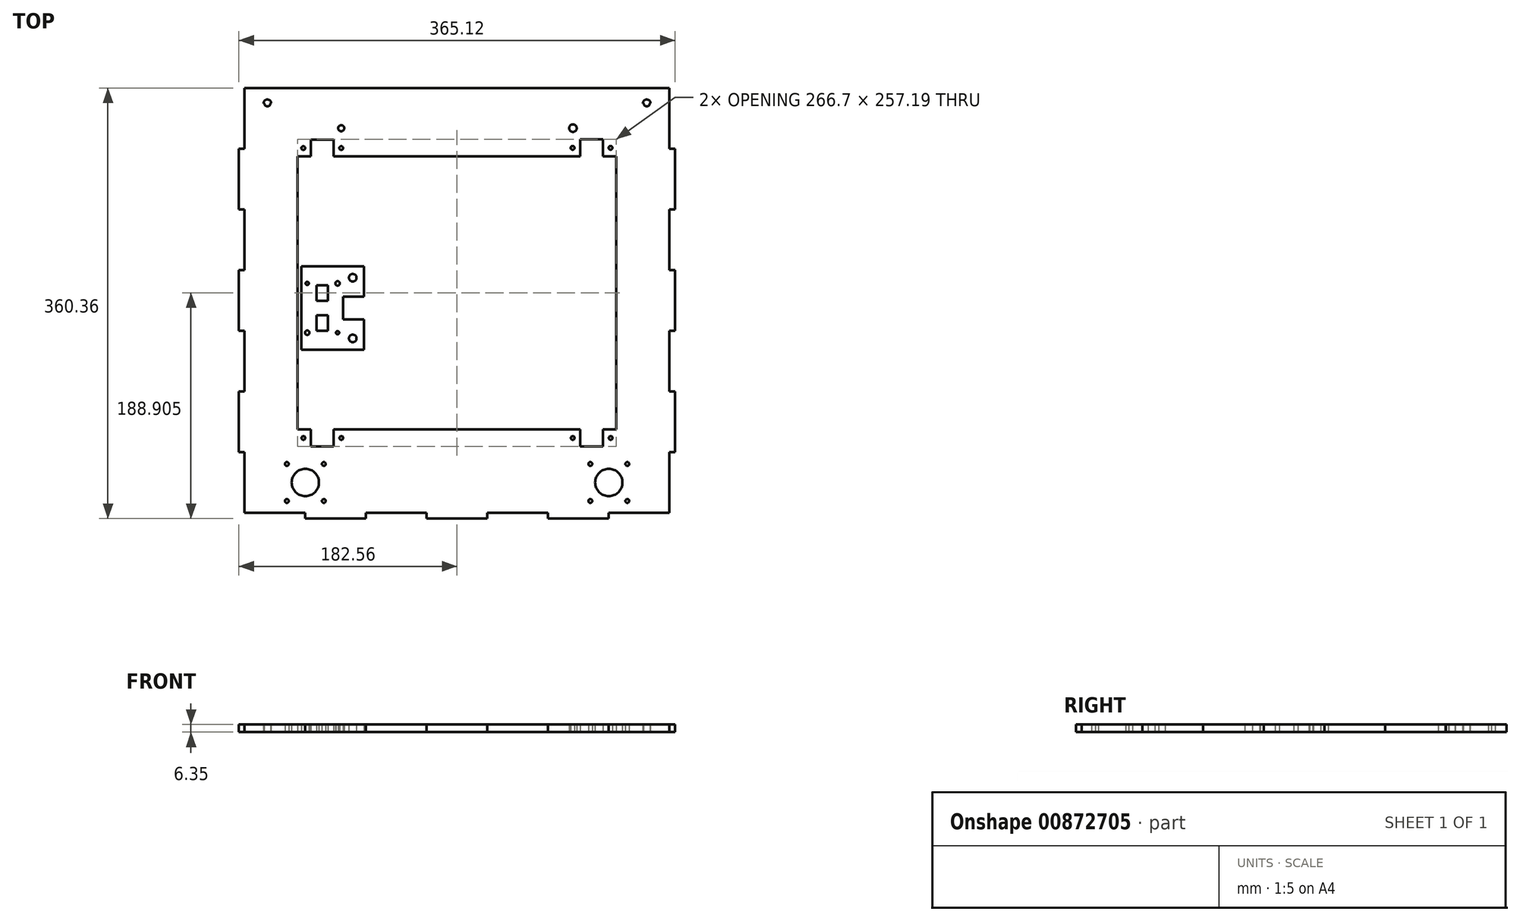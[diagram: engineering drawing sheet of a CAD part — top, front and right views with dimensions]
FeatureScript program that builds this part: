
annotation { "Feature Type Name" : "Feature", "Feature Type Description" : "" }
export const myFeature = defineFeature(function(context is Context, id is Id, definition is map)
    precondition{}
    {
        {
            var Q0;
            Q0=qCreatedBy(makeId("Top.planeOp"),FACE);
            var sketch = newSketch(context, id + "F0", { "sketchPlane" : qUnion([Q0])});
            skLineSegment(sketch, "E0.bottom", {"start": v(-177.8, 171.45) * mm, "end": v(177.8, 171.45) * mm});
            skLineSegment(sketch, "E0.top", {"start": v(-177.8, -171.45) * mm, "end": v(177.8, -171.45) * mm});
            skLineSegment(sketch, "E0.left", {"start": v(-177.8, 171.45) * mm, "end": v(-177.8, -171.45) * mm});
            skLineSegment(sketch, "E0.right", {"start": v(177.8, 171.45) * mm, "end": v(177.8, -171.45) * mm});
            skPoint(sketch, "E0.middle", {"position": v(0, 0) * mm});
            skLineSegment(sketch, "E1.0", {"start": v(-133.35, -101.6) * mm, "end": v(133.35, -101.6) * mm});
            skLineSegment(sketch, "E2.0", {"start": v(-133.35, 127) * mm, "end": v(-133.35, -101.6) * mm});
            skLineSegment(sketch, "E3", {"start": v(0, 171.45) * mm, "end": v(0, -171.45) * mm, "construction": true});
            skLineSegment(sketch, "E4", {"start": v(-177.8, 0) * mm, "end": v(177.8, 0) * mm, "construction": true});
            skLineSegment(sketch, "E5.MirrorCS", {"start": v(133.35, 127) * mm, "end": v(133.35, -101.6) * mm});
            skLineSegment(sketch, "E6.0", {"start": v(-133.35, 127) * mm, "end": v(133.35, 127) * mm});
            skLineSegment(sketch, "E7.bottom", {"start": v(-130.18, 25.4) * mm, "end": v(-95.25, 25.4) * mm});
            skLineSegment(sketch, "E7.top", {"start": v(-130.18, -25.4) * mm, "end": v(-95.25, -25.4) * mm});
            skLineSegment(sketch, "E7.left", {"start": v(-130.18, 25.4) * mm, "end": v(-130.18, -25.4) * mm});
            skLineSegment(sketch, "E7.right", {"start": v(-95.25, 25.4) * mm, "end": v(-95.25, -25.4) * mm});
            skLineSegment(sketch, "E8", {"start": v(-112.71, 25.4) * mm, "end": v(-112.71, -171.45) * mm, "construction": true});
            skLineSegment(sketch, "E9.bottom", {"start": v(-107.95, 6.1) * mm, "end": v(-117.48, 6.1) * mm});
            skLineSegment(sketch, "E9.top", {"start": v(-107.95, 19.05) * mm, "end": v(-117.48, 19.05) * mm});
            skLineSegment(sketch, "E9.left", {"start": v(-107.95, 6.1) * mm, "end": v(-107.95, 19.05) * mm});
            skLineSegment(sketch, "E9.right", {"start": v(-117.48, 6.1) * mm, "end": v(-117.48, 19.05) * mm});
            skPoint(sketch, "E9.middle", {"position": v(-112.71, 12.57) * mm});
            skPoint(sketch, "E10", {"position": v(-95.25, 0) * mm});
            skLineSegment(sketch, "E11.MirrorCS", {"start": v(-117.48, -6.1) * mm, "end": v(-117.48, -19.05) * mm});
            skLineSegment(sketch, "E12.MirrorCS", {"start": v(-107.95, -6.1) * mm, "end": v(-107.95, -19.05) * mm});
            skPoint(sketch, "E13.MirrorP", {"position": v(-112.71, -12.57) * mm});
            skLineSegment(sketch, "E14.MirrorCS", {"start": v(-107.95, -6.1) * mm, "end": v(-117.48, -6.1) * mm});
            skLineSegment(sketch, "E15.MirrorCS", {"start": v(-107.95, -19.05) * mm, "end": v(-117.48, -19.05) * mm});
            skCircle(sketch, "E16", {"center": v(-127, -146.05) * mm, "radius": 11.43 * mm});
            skCircle(sketch, "E17", {"center": v(-111.5, -130.56) * mm, "radius": 1.59 * mm});
            skCircle(sketch, "E18.1.0", {"center": v(-142.5, -130.56) * mm, "radius": 1.59 * mm});
            skCircle(sketch, "E18.2.0", {"center": v(-142.5, -161.54) * mm, "radius": 1.59 * mm});
            skCircle(sketch, "E18.3.0", {"center": v(-111.5, -161.54) * mm, "radius": 1.59 * mm});
            skCircle(sketch, "E19.MirrorC", {"center": v(142.5, -130.56) * mm, "radius": 1.59 * mm});
            skCircle(sketch, "E20.MirrorC", {"center": v(111.5, -130.56) * mm, "radius": 1.59 * mm});
            skCircle(sketch, "E21.MirrorC", {"center": v(142.5, -161.54) * mm, "radius": 1.59 * mm});
            skPoint(sketch, "E22.MirrorP", {"position": v(127, -146.05) * mm});
            skCircle(sketch, "E23.MirrorC", {"center": v(111.5, -161.54) * mm, "radius": 1.59 * mm});
            skCircle(sketch, "E24.MirrorC", {"center": v(127, -146.05) * mm, "radius": 11.43 * mm});
            skPoint(sketch, "E25.orphan", {"position": v(-112.71, -25.4) * mm});
            skCircle(sketch, "E26", {"center": v(-128.59, -108.75) * mm, "radius": 1.59 * mm});
            skCircle(sketch, "E27.MirrorC", {"center": v(-96.84, -108.75) * mm, "radius": 1.59 * mm});
            skLineSegment(sketch, "E28.bottom", {"start": v(-122.24, -101.6) * mm, "end": v(-103.19, -101.6) * mm});
            skLineSegment(sketch, "E28.top", {"start": v(-122.24, -115.9) * mm, "end": v(-103.19, -115.9) * mm});
            skLineSegment(sketch, "E28.left", {"start": v(-122.24, -101.6) * mm, "end": v(-122.24, -115.9) * mm});
            skLineSegment(sketch, "E28.right", {"start": v(-103.19, -101.6) * mm, "end": v(-103.19, -115.9) * mm});
            skPoint(sketch, "E29", {"position": v(-112.71, -115.9) * mm});
            skLineSegment(sketch, "E30.MirrorCS", {"start": v(122.24, -101.6) * mm, "end": v(122.24, -115.9) * mm});
            skCircle(sketch, "E31.MirrorC", {"center": v(96.84, -108.75) * mm, "radius": 1.59 * mm});
            skCircle(sketch, "E32.MirrorC", {"center": v(128.59, -108.75) * mm, "radius": 1.59 * mm});
            skLineSegment(sketch, "E33.MirrorCS", {"start": v(122.24, -101.6) * mm, "end": v(103.19, -101.6) * mm});
            skPoint(sketch, "E34.MirrorP", {"position": v(112.71, -115.9) * mm});
            skLineSegment(sketch, "E35.MirrorCS", {"start": v(103.19, -101.6) * mm, "end": v(103.19, -115.9) * mm});
            skLineSegment(sketch, "E36.MirrorCS", {"start": v(122.24, -115.9) * mm, "end": v(103.19, -115.9) * mm});
            skLineSegment(sketch, "E37", {"start": v(133.35, 12.7) * mm, "end": v(-133.35, 12.57) * mm, "construction": true});
            skCircle(sketch, "E38.MirrorC", {"center": v(-128.7, 133.9) * mm, "radius": 1.59 * mm});
            skLineSegment(sketch, "E39.MirrorCS", {"start": v(-122.36, 141.06) * mm, "end": v(-103.3, 141.07) * mm});
            skLineSegment(sketch, "E40.MirrorCS", {"start": v(-122.35, 126.76) * mm, "end": v(-103.3, 126.77) * mm});
            skCircle(sketch, "E41.MirrorC", {"center": v(128.47, 134.15) * mm, "radius": 1.59 * mm});
            skLineSegment(sketch, "E42.MirrorCS", {"start": v(-122.35, 126.76) * mm, "end": v(-122.36, 141.06) * mm});
            skCircle(sketch, "E43.MirrorC", {"center": v(-96.95, 133.93) * mm, "radius": 1.59 * mm});
            skLineSegment(sketch, "E44.MirrorCS", {"start": v(122.12, 141.29) * mm, "end": v(103.07, 141.27) * mm});
            skCircle(sketch, "E45.MirrorC", {"center": v(96.72, 134.12) * mm, "radius": 1.59 * mm});
            skLineSegment(sketch, "E46.MirrorCS", {"start": v(122.13, 126.99) * mm, "end": v(103.08, 126.97) * mm});
            skPoint(sketch, "E47.MirrorP", {"position": v(-112.83, 141.07) * mm});
            skPoint(sketch, "E48.MirrorP", {"position": v(112.6, 141.28) * mm});
            skLineSegment(sketch, "E49.MirrorCS", {"start": v(-133.46, 126.75) * mm, "end": v(133.24, 127) * mm});
            skLineSegment(sketch, "E50.MirrorCS", {"start": v(103.08, 126.97) * mm, "end": v(103.07, 141.27) * mm});
            skLineSegment(sketch, "E51.MirrorCS", {"start": v(-103.3, 126.77) * mm, "end": v(-103.3, 141.07) * mm});
            skLineSegment(sketch, "E52.MirrorCS", {"start": v(122.13, 126.99) * mm, "end": v(122.12, 141.29) * mm});
            skLineSegment(sketch, "E53.bottom", {"start": v(-95.25, -9.53) * mm, "end": v(-77.79, -9.53) * mm});
            skLineSegment(sketch, "E53.top", {"start": v(-95.25, 9.52) * mm, "end": v(-77.79, 9.52) * mm});
            skLineSegment(sketch, "E53.left", {"start": v(-95.25, -9.53) * mm, "end": v(-95.25, 9.52) * mm});
            skLineSegment(sketch, "E53.right", {"start": v(-77.79, -9.53) * mm, "end": v(-77.79, 9.52) * mm});
            skPoint(sketch, "E54", {"position": v(-65.09, 0) * mm});
            skLineSegment(sketch, "E55.bottom", {"start": v(-95.25, -25.4) * mm, "end": v(-77.79, -25.4) * mm});
            skLineSegment(sketch, "E55.top", {"start": v(-95.25, 25.4) * mm, "end": v(-77.79, 25.4) * mm});
            skLineSegment(sketch, "E55.left", {"start": v(-95.25, -25.4) * mm, "end": v(-95.25, 25.4) * mm});
            skLineSegment(sketch, "E55.right", {"start": v(-77.79, -25.4) * mm, "end": v(-77.79, 25.4) * mm});
            skLineSegment(sketch, "E56.0", {"start": v(-100.01, 34.92) * mm, "end": v(-77.79, 34.92) * mm});
            skLineSegment(sketch, "E56.1", {"start": v(-130.18, 34.92) * mm, "end": v(-100.01, 34.92) * mm});
            skLineSegment(sketch, "E57", {"start": v(-77.79, 34.92) * mm, "end": v(-77.79, 25.4) * mm});
            skLineSegment(sketch, "E58", {"start": v(-130.18, 25.4) * mm, "end": v(-130.18, 34.92) * mm});
            skLineSegment(sketch, "E59.MirrorCS", {"start": v(-130.18, -25.4) * mm, "end": v(-130.18, -34.92) * mm});
            skLineSegment(sketch, "E60.MirrorCS", {"start": v(-100.01, -34.93) * mm, "end": v(-77.79, -34.93) * mm});
            skLineSegment(sketch, "E61.MirrorCS", {"start": v(-130.18, -34.93) * mm, "end": v(-100.01, -34.93) * mm});
            skLineSegment(sketch, "E62.MirrorCS", {"start": v(-77.79, -34.92) * mm, "end": v(-77.79, -25.4) * mm});
            skCircle(sketch, "E63", {"center": v(-87.31, 25.4) * mm, "radius": 3.18 * mm});
            skCircle(sketch, "E64.MirrorC", {"center": v(-87.31, -25.4) * mm, "radius": 3.18 * mm});
            skCircle(sketch, "E65", {"center": v(-125.41, 20.64) * mm, "radius": 1.84 * mm});
            skCircle(sketch, "E66.MirrorC", {"center": v(-100.01, 20.64) * mm, "radius": 1.84 * mm});
            skCircle(sketch, "E67.MirrorC", {"center": v(-125.41, -20.64) * mm, "radius": 1.84 * mm});
            skCircle(sketch, "E68.MirrorC", {"center": v(-100.01, -20.64) * mm, "radius": 1.84 * mm});
            skCircle(sketch, "E69", {"center": v(-158.75, 171.45) * mm, "radius": 3.18 * mm});
            skCircle(sketch, "E70", {"center": v(-96.95, 150.6) * mm, "radius": 3.18 * mm});
            skCircle(sketch, "E71.MirrorC", {"center": v(96.95, 150.6) * mm, "radius": 3.18 * mm});
            skCircle(sketch, "E72.MirrorC", {"center": v(158.75, 171.45) * mm, "radius": 3.18 * mm});
            skLineSegment(sketch, "E73.0", {"start": v(-177.8, 184.15) * mm, "end": v(177.8, 184.15) * mm});
            skLineSegment(sketch, "E74", {"start": v(-177.8, 171.45) * mm, "end": v(-177.8, 184.15) * mm});
            skLineSegment(sketch, "E75", {"start": v(177.8, 171.45) * mm, "end": v(177.8, 184.15) * mm});
            skLineSegment(sketch, "E76.bottom", {"start": v(-177.8, 133.35) * mm, "end": v(-182.56, 133.35) * mm});
            skLineSegment(sketch, "E76.top", {"start": v(-177.8, 82.55) * mm, "end": v(-182.56, 82.55) * mm});
            skLineSegment(sketch, "E76.left", {"start": v(-177.8, 133.35) * mm, "end": v(-177.8, 82.55) * mm});
            skLineSegment(sketch, "E76.right", {"start": v(-182.56, 133.35) * mm, "end": v(-182.56, 82.55) * mm});
            skLineSegment(sketch, "E77.bottom", {"start": v(-177.8, 31.75) * mm, "end": v(-182.56, 31.75) * mm});
            skLineSegment(sketch, "E77.top", {"start": v(-177.8, -19.05) * mm, "end": v(-182.56, -19.05) * mm});
            skLineSegment(sketch, "E77.left", {"start": v(-177.8, 31.75) * mm, "end": v(-177.8, -19.05) * mm});
            skLineSegment(sketch, "E77.right", {"start": v(-182.56, 31.75) * mm, "end": v(-182.56, -19.05) * mm});
            skLineSegment(sketch, "E78.bottom", {"start": v(-177.8, -69.85) * mm, "end": v(-182.56, -69.85) * mm});
            skLineSegment(sketch, "E78.top", {"start": v(-177.8, -120.65) * mm, "end": v(-182.56, -120.65) * mm});
            skLineSegment(sketch, "E78.left", {"start": v(-177.8, -69.85) * mm, "end": v(-177.8, -120.65) * mm});
            skLineSegment(sketch, "E78.right", {"start": v(-182.56, -69.85) * mm, "end": v(-182.56, -120.65) * mm});
            skLineSegment(sketch, "E79.MirrorCS", {"start": v(177.8, -120.65) * mm, "end": v(182.56, -120.65) * mm});
            skLineSegment(sketch, "E80.MirrorCS", {"start": v(177.8, 31.75) * mm, "end": v(182.56, 31.75) * mm});
            skLineSegment(sketch, "E81.MirrorCS", {"start": v(177.8, -19.05) * mm, "end": v(182.56, -19.05) * mm});
            skLineSegment(sketch, "E82.MirrorCS", {"start": v(177.8, 82.55) * mm, "end": v(182.56, 82.55) * mm});
            skLineSegment(sketch, "E83.MirrorCS", {"start": v(177.8, -69.85) * mm, "end": v(182.56, -69.85) * mm});
            skLineSegment(sketch, "E84.MirrorCS", {"start": v(177.8, 133.35) * mm, "end": v(182.56, 133.35) * mm});
            skLineSegment(sketch, "E85.MirrorCS", {"start": v(182.56, 133.35) * mm, "end": v(182.56, 82.55) * mm});
            skLineSegment(sketch, "E86.MirrorCS", {"start": v(177.8, 31.75) * mm, "end": v(177.8, -19.05) * mm});
            skLineSegment(sketch, "E87.MirrorCS", {"start": v(182.56, 31.75) * mm, "end": v(182.56, -19.05) * mm});
            skLineSegment(sketch, "E88.MirrorCS", {"start": v(177.8, 133.35) * mm, "end": v(177.8, 82.55) * mm});
            skLineSegment(sketch, "E89.MirrorCS", {"start": v(177.8, -69.85) * mm, "end": v(177.8, -120.65) * mm});
            skLineSegment(sketch, "E90.MirrorCS", {"start": v(182.56, -69.85) * mm, "end": v(182.56, -120.65) * mm});
            skLineSegment(sketch, "E91.bottom", {"start": v(-127, 184.15) * mm, "end": v(-76.2, 184.15) * mm});
            skLineSegment(sketch, "E91.top", {"start": v(-127, 188.91) * mm, "end": v(-76.2, 188.91) * mm});
            skLineSegment(sketch, "E91.left", {"start": v(-127, 184.15) * mm, "end": v(-127, 188.91) * mm});
            skLineSegment(sketch, "E91.right", {"start": v(-76.2, 184.15) * mm, "end": v(-76.2, 188.91) * mm});
            skLineSegment(sketch, "E92.bottom", {"start": v(-25.4, 184.15) * mm, "end": v(25.4, 184.15) * mm});
            skLineSegment(sketch, "E92.top", {"start": v(-25.4, 188.91) * mm, "end": v(25.4, 188.91) * mm});
            skLineSegment(sketch, "E92.left", {"start": v(-25.4, 184.15) * mm, "end": v(-25.4, 188.91) * mm});
            skLineSegment(sketch, "E92.right", {"start": v(25.4, 184.15) * mm, "end": v(25.4, 188.91) * mm});
            skLineSegment(sketch, "E93.bottom", {"start": v(76.2, 184.15) * mm, "end": v(127, 184.15) * mm});
            skLineSegment(sketch, "E93.top", {"start": v(76.2, 188.91) * mm, "end": v(127, 188.91) * mm});
            skLineSegment(sketch, "E93.left", {"start": v(76.2, 184.15) * mm, "end": v(76.2, 188.91) * mm});
            skLineSegment(sketch, "E93.right", {"start": v(127, 184.15) * mm, "end": v(127, 188.91) * mm});
            skLineSegment(sketch, "E94", {"start": v(177.8, 184.15) * mm, "end": v(177.8, -171.45) * mm, "construction": true});
            skLineSegment(sketch, "E95", {"start": v(177.8, 6.35) * mm, "end": v(-210.69, 6.35) * mm, "construction": true});
            skLineSegment(sketch, "E96.MirrorCS", {"start": v(25.4, -171.45) * mm, "end": v(25.4, -176.21) * mm});
            skLineSegment(sketch, "E97.MirrorCS", {"start": v(76.2, -171.45) * mm, "end": v(76.2, -176.21) * mm});
            skLineSegment(sketch, "E98.MirrorCS", {"start": v(127, -171.45) * mm, "end": v(127, -176.21) * mm});
            skLineSegment(sketch, "E99.MirrorCS", {"start": v(-127, -171.45) * mm, "end": v(-127, -176.21) * mm});
            skLineSegment(sketch, "E100.MirrorCS", {"start": v(-25.4, -171.45) * mm, "end": v(-25.4, -176.21) * mm});
            skLineSegment(sketch, "E101.MirrorCS", {"start": v(-76.2, -171.45) * mm, "end": v(-76.2, -176.21) * mm});
            skLineSegment(sketch, "E102.MirrorCS", {"start": v(76.2, -171.45) * mm, "end": v(127, -171.45) * mm});
            skLineSegment(sketch, "E103.MirrorCS", {"start": v(-127, -176.21) * mm, "end": v(-76.2, -176.21) * mm});
            skLineSegment(sketch, "E104.MirrorCS", {"start": v(76.2, -176.21) * mm, "end": v(127, -176.21) * mm});
            skLineSegment(sketch, "E105.MirrorCS", {"start": v(-25.4, -171.45) * mm, "end": v(25.4, -171.45) * mm});
            skLineSegment(sketch, "E106.MirrorCS", {"start": v(-25.4, -176.21) * mm, "end": v(25.4, -176.21) * mm});
            skLineSegment(sketch, "E107.MirrorCS", {"start": v(-127, -171.45) * mm, "end": v(-76.2, -171.45) * mm});
            skLineSegment(sketch, "E108.bottom", {"start": v(-22.23, 126.85) * mm, "end": v(22.22, 126.85) * mm});
            skLineSegment(sketch, "E108.top", {"start": v(-22.23, 168.13) * mm, "end": v(22.22, 168.13) * mm});
            skLineSegment(sketch, "E108.left", {"start": v(-22.23, 126.85) * mm, "end": v(-22.23, 168.13) * mm});
            skLineSegment(sketch, "E108.right", {"start": v(22.22, 126.85) * mm, "end": v(22.22, 168.13) * mm});
            skPoint(sketch, "E109", {"position": v(0, 168.13) * mm});
            skSolve(sketch);
        }
        {
            var Q0;
            Q0=makeQuery(id+"F0.imprint","IMPRINT",FACE,{"disambiguationData":[TD([[makeQuery(id+"F0.imprint","IMPRINT",EDGE,{"derivedFrom":sQuery(id+"F0.wireOp",EDGE,"E0.bottom")}),-1.0]])]});
            var Q1;
            {var subQ0=sQuery(id+"F0.wireOp",EDGE,"E7.bottom");Q1=makeQuery(id+"F0.imprint","IMPRINT",FACE,{"disambiguationData":[TD([[makeQuery(id+"F0.imprint","IMPRINT",EDGE,{"derivedFrom":subQ0}),-1.0]])]});}
            var Q2;
            {var subQ1=sQuery(id+"F0.wireOp",EDGE,"E53.bottom");Q2=makeQuery(id+"F0.imprint","IMPRINT",FACE,{"disambiguationData":[TD([[makeQuery(id+"F0.imprint","IMPRINT",EDGE,{"derivedFrom":subQ1}),-1.0]])]});}
            var Q3;
            {var subQ7=sQuery(id+"F0.wireOp",EDGE,"E53.top");Q3=makeQuery(id+"F0.imprint","IMPRINT",FACE,{"disambiguationData":[TD([[makeQuery(id+"F0.imprint","IMPRINT",EDGE,{"derivedFrom":subQ7}),1.0]])]});}
            var Q4;
            {var subQ0=sQuery(id+"F0.wireOp",EDGE,"E7.top");Q4=makeQuery(id+"F0.imprint","IMPRINT",FACE,{"disambiguationData":[TD([[makeQuery(id+"F0.imprint","IMPRINT",EDGE,{"derivedFrom":subQ0}),-1.0]])]});}
            var Q5;
            {var subQ1=sQuery(id+"F0.wireOp",EDGE,"E7.bottom");Q5=makeQuery(id+"F0.imprint","IMPRINT",FACE,{"disambiguationData":[TD([[makeQuery(id+"F0.imprint","IMPRINT",EDGE,{"derivedFrom":subQ1}),1.0]])]});}
            var Q6;
            {var subQ0=sQuery(id+"F0.wireOp",EDGE,"E63");var subQ1=sQuery(id+"F0.wireOp",EDGE,"E55.top");var subQ2=makeQuery(id+"F0.imprint","INTERSECT",VERTEX,{"disambiguationData":[OD(0.0)],"derivedFrom":[subQ1,subQ0]});Q6=makeQuery(id+"F0.imprint","IMPRINT",FACE,{"disambiguationData":[TD([[makeQuery(id+"F0.imprint","IMPRINT",EDGE,{"disambiguationData":[TD([[subQ2,-1.0]])],"derivedFrom":subQ1}),-1.0]])]});}
            var Q7;
            {var subQ0=sQuery(id+"F0.wireOp",EDGE,"E64.MirrorC");var subQ1=sQuery(id+"F0.wireOp",EDGE,"E55.bottom");var subQ2=makeQuery(id+"F0.imprint","INTERSECT",VERTEX,{"disambiguationData":[OD(0.0)],"derivedFrom":[subQ1,subQ0]});Q7=makeQuery(id+"F0.imprint","IMPRINT",FACE,{"disambiguationData":[TD([[makeQuery(id+"F0.imprint","IMPRINT",EDGE,{"disambiguationData":[TD([[subQ2,-1.0]])],"derivedFrom":subQ1}),-1.0]])]});}
            var Q8;
            Q8=makeQuery(id+"F0.imprint","IMPRINT",FACE,{"disambiguationData":[TD([[makeQuery(id+"F0.imprint","IMPRINT",EDGE,{"derivedFrom":sQuery(id+"F0.wireOp",EDGE,"E66.MirrorC")}),-1.0]])]});
            var Q9;
            Q9=makeQuery(id+"F0.imprint","IMPRINT",FACE,{"disambiguationData":[TD([[makeQuery(id+"F0.imprint","IMPRINT",EDGE,{"derivedFrom":sQuery(id+"F0.wireOp",EDGE,"E65")}),1.0]])]});
            var Q10;
            Q10=makeQuery(id+"F0.imprint","IMPRINT",FACE,{"disambiguationData":[TD([[makeQuery(id+"F0.imprint","IMPRINT",EDGE,{"derivedFrom":sQuery(id+"F0.wireOp",EDGE,"E67.MirrorC")}),-1.0]])]});
            var Q11;
            {var subQ0=sQuery(id+"F0.wireOp",EDGE,"E63");var subQ1=sQuery(id+"F0.wireOp",EDGE,"E55.top");var subQ2=makeQuery(id+"F0.imprint","INTERSECT",VERTEX,{"disambiguationData":[OD(0.0)],"derivedFrom":[subQ1,subQ0]});Q11=makeQuery(id+"F0.imprint","IMPRINT",FACE,{"disambiguationData":[TD([[makeQuery(id+"F0.imprint","IMPRINT",EDGE,{"disambiguationData":[TD([[subQ2,-1.0]])],"derivedFrom":subQ1}),1.0]])]});}
            var Q12;
            Q12=makeQuery(id+"F0.imprint","IMPRINT",FACE,{"disambiguationData":[TD([[makeQuery(id+"F0.imprint","IMPRINT",EDGE,{"derivedFrom":sQuery(id+"F0.wireOp",EDGE,"E68.MirrorC")}),1.0]])]});
            var Q13;
            {var subQ0=sQuery(id+"F0.wireOp",EDGE,"E64.MirrorC");var subQ1=sQuery(id+"F0.wireOp",EDGE,"E55.bottom");var subQ2=makeQuery(id+"F0.imprint","INTERSECT",VERTEX,{"disambiguationData":[OD(0.0)],"derivedFrom":[subQ1,subQ0]});Q13=makeQuery(id+"F0.imprint","IMPRINT",FACE,{"disambiguationData":[TD([[makeQuery(id+"F0.imprint","IMPRINT",EDGE,{"disambiguationData":[TD([[subQ2,-1.0]])],"derivedFrom":subQ1}),1.0]])]});}
            var Q14;
            Q14=makeQuery(id+"F0.imprint","IMPRINT",FACE,{"disambiguationData":[TD([[makeQuery(id+"F0.imprint","IMPRINT",EDGE,{"derivedFrom":sQuery(id+"F0.wireOp",EDGE,"E0.top")}),1.0]])]});
            var Q15;
            Q15=makeQuery(id+"F0.imprint","IMPRINT",FACE,{"disambiguationData":[TD([[makeQuery(id+"F0.imprint","IMPRINT",EDGE,{"derivedFrom":sQuery(id+"F0.wireOp",EDGE,"E73.0")}),-1.0]])]});
            var Q16;
            {var subQ0=sQuery(id+"F0.wireOp",EDGE,"E69");var subQ1=sQuery(id+"F0.wireOp",EDGE,"E0.bottom");var subQ2=makeQuery(id+"F0.imprint","INTERSECT",VERTEX,{"disambiguationData":[OD(0.0)],"derivedFrom":[subQ1,subQ0]});Q16=makeQuery(id+"F0.imprint","IMPRINT",FACE,{"disambiguationData":[TD([[makeQuery(id+"F0.imprint","IMPRINT",EDGE,{"disambiguationData":[TD([[subQ2,-1.0]])],"derivedFrom":subQ1}),1.0]])]});}
            var Q17;
            {var subQ0=sQuery(id+"F0.wireOp",EDGE,"E72.MirrorC");var subQ1=sQuery(id+"F0.wireOp",EDGE,"E0.bottom");var subQ2=makeQuery(id+"F0.imprint","INTERSECT",VERTEX,{"disambiguationData":[OD(0.0)],"derivedFrom":[subQ1,subQ0]});Q17=makeQuery(id+"F0.imprint","IMPRINT",FACE,{"disambiguationData":[TD([[makeQuery(id+"F0.imprint","IMPRINT",EDGE,{"disambiguationData":[TD([[subQ2,-1.0]])],"derivedFrom":subQ1}),1.0]])]});}
            var Q18;
            Q18=makeQuery(id+"F0.imprint","IMPRINT",FACE,{"disambiguationData":[TD([[makeQuery(id+"F0.imprint","IMPRINT",EDGE,{"derivedFrom":sQuery(id+"F0.wireOp",EDGE,"E70")}),1.0]])]});
            var Q19;
            Q19=makeQuery(id+"F0.imprint","IMPRINT",FACE,{"disambiguationData":[TD([[makeQuery(id+"F0.imprint","IMPRINT",EDGE,{"derivedFrom":sQuery(id+"F0.wireOp",EDGE,"E71.MirrorC")}),-1.0]])]});
            var Q20;
            Q20=makeQuery(id+"F0.imprint","IMPRINT",FACE,{"disambiguationData":[TD([[makeQuery(id+"F0.imprint","IMPRINT",EDGE,{"derivedFrom":sQuery(id+"F0.wireOp",EDGE,"E76.bottom")}),1.0]])]});
            var Q21;
            Q21=makeQuery(id+"F0.imprint","IMPRINT",FACE,{"disambiguationData":[TD([[makeQuery(id+"F0.imprint","IMPRINT",EDGE,{"derivedFrom":sQuery(id+"F0.wireOp",EDGE,"E91.bottom")}),1.0]])]});
            var Q22;
            Q22=makeQuery(id+"F0.imprint","IMPRINT",FACE,{"disambiguationData":[TD([[makeQuery(id+"F0.imprint","IMPRINT",EDGE,{"derivedFrom":sQuery(id+"F0.wireOp",EDGE,"E92.bottom")}),1.0]])]});
            var Q23;
            Q23=makeQuery(id+"F0.imprint","IMPRINT",FACE,{"disambiguationData":[TD([[makeQuery(id+"F0.imprint","IMPRINT",EDGE,{"derivedFrom":sQuery(id+"F0.wireOp",EDGE,"E93.bottom")}),1.0]])]});
            var Q24;
            Q24=makeQuery(id+"F0.imprint","IMPRINT",FACE,{"disambiguationData":[TD([[makeQuery(id+"F0.imprint","IMPRINT",EDGE,{"derivedFrom":sQuery(id+"F0.wireOp",EDGE,"E82.MirrorCS")}),1.0]])]});
            var Q25;
            Q25=makeQuery(id+"F0.imprint","IMPRINT",FACE,{"disambiguationData":[TD([[makeQuery(id+"F0.imprint","IMPRINT",EDGE,{"derivedFrom":sQuery(id+"F0.wireOp",EDGE,"E80.MirrorCS")}),-1.0]])]});
            var Q26;
            Q26=makeQuery(id+"F0.imprint","IMPRINT",FACE,{"disambiguationData":[TD([[makeQuery(id+"F0.imprint","IMPRINT",EDGE,{"derivedFrom":sQuery(id+"F0.wireOp",EDGE,"E79.MirrorCS")}),1.0]])]});
            var Q27;
            Q27=makeQuery(id+"F0.imprint","IMPRINT",FACE,{"disambiguationData":[TD([[makeQuery(id+"F0.imprint","IMPRINT",EDGE,{"derivedFrom":sQuery(id+"F0.wireOp",EDGE,"E78.bottom")}),1.0]])]});
            var Q28;
            Q28=makeQuery(id+"F0.imprint","IMPRINT",FACE,{"disambiguationData":[TD([[makeQuery(id+"F0.imprint","IMPRINT",EDGE,{"derivedFrom":sQuery(id+"F0.wireOp",EDGE,"E77.bottom")}),1.0]])]});
            var Q29;
            Q29=makeQuery(id+"F0.imprint","IMPRINT",FACE,{"disambiguationData":[TD([[makeQuery(id+"F0.imprint","IMPRINT",EDGE,{"derivedFrom":sQuery(id+"F0.wireOp",EDGE,"E99.MirrorCS")}),1.0]])]});
            var Q30;
            Q30=makeQuery(id+"F0.imprint","IMPRINT",FACE,{"disambiguationData":[TD([[makeQuery(id+"F0.imprint","IMPRINT",EDGE,{"derivedFrom":sQuery(id+"F0.wireOp",EDGE,"E96.MirrorCS")}),-1.0]])]});
            var Q31;
            Q31=makeQuery(id+"F0.imprint","IMPRINT",FACE,{"disambiguationData":[TD([[makeQuery(id+"F0.imprint","IMPRINT",EDGE,{"derivedFrom":sQuery(id+"F0.wireOp",EDGE,"E97.MirrorCS")}),1.0]])]});
            var Q32;
            {var subQ5=sQuery(id+"F0.wireOp",EDGE,"E108.top");Q32=makeQuery(id+"F0.imprint","IMPRINT",FACE,{"disambiguationData":[TD([[makeQuery(id+"F0.imprint","IMPRINT",EDGE,{"derivedFrom":subQ5}),-1.0]])]});}
            extrude(context, id + "F1", {"entities" : qUnion([Q0, Q1, Q2, Q3, Q4, Q5, Q6, Q7, Q8, Q9, Q10, Q11, Q12, Q13, Q14, Q15, Q16, Q17, Q18, Q19, Q20, Q21, Q22, Q23, Q24, Q25, Q26, Q27, Q28, Q29, Q30, Q31, Q32]), "depth" : 6.35 * mm, "offsetDistance" : 25.4 * mm});
        }
        {
            var Q0;
            Q0=sQuery(id+"F0.wireOp",VERTEX,"E65.center");
            var Q1;
            Q1=sQuery(id+"F0.wireOp",VERTEX,"E66.MirrorC.center");
            var Q2;
            Q2=sQuery(id+"F0.wireOp",VERTEX,"E68.MirrorC.center");
            var Q3;
            Q3=sQuery(id+"F0.wireOp",VERTEX,"E67.MirrorC.center");
            var Q4;
            Q4=makeQuery(id+"F1.opExtrude","SWEPT_BODY",BODY,{"disambiguationData":[OSD([sQuery(id+"F0.wireOp",EDGE,"E7.left"),sQuery(id+"F0.wireOp",EDGE,"E9.bottom"),sQuery(id+"F0.wireOp",EDGE,"E9.top"),sQuery(id+"F0.wireOp",EDGE,"E9.left"),sQuery(id+"F0.wireOp",EDGE,"E9.right"),sQuery(id+"F0.wireOp",EDGE,"E11.MirrorCS"),sQuery(id+"F0.wireOp",EDGE,"E12.MirrorCS"),sQuery(id+"F0.wireOp",EDGE,"E14.MirrorCS"),sQuery(id+"F0.wireOp",EDGE,"E15.MirrorCS"),sQuery(id+"F0.wireOp",EDGE,"E53.bottom"),sQuery(id+"F0.wireOp",EDGE,"E53.top"),sQuery(id+"F0.wireOp",EDGE,"E55.left"),sQuery(id+"F0.wireOp",EDGE,"E55.right"),sQuery(id+"F0.wireOp",EDGE,"E56.0"),sQuery(id+"F0.wireOp",EDGE,"E56.1"),sQuery(id+"F0.wireOp",EDGE,"E57"),sQuery(id+"F0.wireOp",EDGE,"E58"),sQuery(id+"F0.wireOp",EDGE,"E59.MirrorCS"),sQuery(id+"F0.wireOp",EDGE,"E60.MirrorCS"),sQuery(id+"F0.wireOp",EDGE,"E61.MirrorCS"),sQuery(id+"F0.wireOp",EDGE,"E62.MirrorCS")])]});
            hole(context, id + "F2", {"style" : HoleStyle.SIMPLE, "endStyle" : HoleEndStyle.THROUGH, "oppositeDirection" : true, "standardTappedOrClearance" : lookupTablePath({ "standard" : "ANSI", "engagement" : "75%", "pitch" : "32 tpi", "size" : "#6", "type" : "Tapped" }), "standardBlindInLast" : lookupTablePath({ "standard" : "ANSI", "engagement" : "75%", "pitch" : "32 tpi", "size" : "#6", "type" : "Tapped" }), "holeDiameter" : 2.7 * mm, "majorDiameter" : 3.5 * mm, "showTappedDepth" : true, "isTappedThrough" : true, "tappedDepth" : 12.7 * mm, "tapClearance" : 3, "locations" : qUnion([Q0, Q1, Q2, Q3]), "scope" : qUnion([Q4])});
        }
        {
            var Q0;
            Q0=sQuery(id+"F0.wireOp",VERTEX,"E63.center");
            var Q1;
            Q1=sQuery(id+"F0.wireOp",VERTEX,"E64.MirrorC.center");
            var Q2;
            Q2=makeQuery(id+"F1.opExtrude","SWEPT_BODY",BODY,{"disambiguationData":[OSD([sQuery(id+"F0.wireOp",EDGE,"E7.left"),sQuery(id+"F0.wireOp",EDGE,"E9.bottom"),sQuery(id+"F0.wireOp",EDGE,"E9.top"),sQuery(id+"F0.wireOp",EDGE,"E9.left"),sQuery(id+"F0.wireOp",EDGE,"E9.right"),sQuery(id+"F0.wireOp",EDGE,"E11.MirrorCS"),sQuery(id+"F0.wireOp",EDGE,"E12.MirrorCS"),sQuery(id+"F0.wireOp",EDGE,"E14.MirrorCS"),sQuery(id+"F0.wireOp",EDGE,"E15.MirrorCS"),sQuery(id+"F0.wireOp",EDGE,"E53.bottom"),sQuery(id+"F0.wireOp",EDGE,"E53.top"),sQuery(id+"F0.wireOp",EDGE,"E55.left"),sQuery(id+"F0.wireOp",EDGE,"E55.right"),sQuery(id+"F0.wireOp",EDGE,"E56.0"),sQuery(id+"F0.wireOp",EDGE,"E56.1"),sQuery(id+"F0.wireOp",EDGE,"E57"),sQuery(id+"F0.wireOp",EDGE,"E58"),sQuery(id+"F0.wireOp",EDGE,"E59.MirrorCS"),sQuery(id+"F0.wireOp",EDGE,"E60.MirrorCS"),sQuery(id+"F0.wireOp",EDGE,"E61.MirrorCS"),sQuery(id+"F0.wireOp",EDGE,"E62.MirrorCS")])]});
            hole(context, id + "F3", {"style" : HoleStyle.SIMPLE, "endStyle" : HoleEndStyle.THROUGH, "oppositeDirection" : true, "standardTappedOrClearance" : lookupTablePath({ "standard" : "ANSI", "engagement" : "75%", "pitch" : "20 tpi", "size" : "1/4", "type" : "Tapped" }), "standardBlindInLast" : lookupTablePath({ "standard" : "ANSI", "engagement" : "75%", "pitch" : "20 tpi", "size" : "1/4", "type" : "Tapped" }), "holeDiameter" : 5.1 * mm, "majorDiameter" : 6.35 * mm, "showTappedDepth" : true, "isTappedThrough" : true, "tappedDepth" : 12.7 * mm, "tapClearance" : 3, "locations" : qUnion([Q0, Q1]), "scope" : qUnion([Q2])});
        }
        {
            var Q0;
            Q0=sQuery(id+"F0.wireOp",VERTEX,"E69.center");
            var Q1;
            Q1=sQuery(id+"F0.wireOp",VERTEX,"E70.center");
            var Q2;
            Q2=sQuery(id+"F0.wireOp",VERTEX,"E71.MirrorC.center");
            var Q3;
            Q3=sQuery(id+"F0.wireOp",VERTEX,"E72.MirrorC.center");
            var Q4;
            Q4=makeQuery(id+"F1.opExtrude","SWEPT_BODY",BODY,{"disambiguationData":[OSD([sQuery(id+"F0.wireOp",EDGE,"E0.top"),sQuery(id+"F0.wireOp",EDGE,"E0.left"),sQuery(id+"F0.wireOp",EDGE,"E0.right"),sQuery(id+"F0.wireOp",EDGE,"E1.0"),sQuery(id+"F0.wireOp",EDGE,"E2.0"),sQuery(id+"F0.wireOp",EDGE,"E5.MirrorCS"),sQuery(id+"F0.wireOp",EDGE,"E6.0"),sQuery(id+"F0.wireOp",EDGE,"E16"),sQuery(id+"F0.wireOp",EDGE,"E17"),sQuery(id+"F0.wireOp",EDGE,"E18.1.0"),sQuery(id+"F0.wireOp",EDGE,"E18.2.0"),sQuery(id+"F0.wireOp",EDGE,"E18.3.0"),sQuery(id+"F0.wireOp",EDGE,"E19.MirrorC"),sQuery(id+"F0.wireOp",EDGE,"E20.MirrorC"),sQuery(id+"F0.wireOp",EDGE,"E21.MirrorC"),sQuery(id+"F0.wireOp",EDGE,"E23.MirrorC"),sQuery(id+"F0.wireOp",EDGE,"E24.MirrorC"),sQuery(id+"F0.wireOp",EDGE,"E26"),sQuery(id+"F0.wireOp",EDGE,"E27.MirrorC"),sQuery(id+"F0.wireOp",EDGE,"E28.top"),sQuery(id+"F0.wireOp",EDGE,"E28.left"),sQuery(id+"F0.wireOp",EDGE,"E28.right"),sQuery(id+"F0.wireOp",EDGE,"E30.MirrorCS"),sQuery(id+"F0.wireOp",EDGE,"E31.MirrorC"),sQuery(id+"F0.wireOp",EDGE,"E32.MirrorC"),sQuery(id+"F0.wireOp",EDGE,"E35.MirrorCS"),sQuery(id+"F0.wireOp",EDGE,"E36.MirrorCS"),sQuery(id+"F0.wireOp",EDGE,"E38.MirrorC"),sQuery(id+"F0.wireOp",EDGE,"E39.MirrorCS"),sQuery(id+"F0.wireOp",EDGE,"E41.MirrorC"),sQuery(id+"F0.wireOp",EDGE,"E42.MirrorCS"),sQuery(id+"F0.wireOp",EDGE,"E43.MirrorC"),sQuery(id+"F0.wireOp",EDGE,"E44.MirrorCS"),sQuery(id+"F0.wireOp",EDGE,"E45.MirrorC"),sQuery(id+"F0.wireOp",EDGE,"E50.MirrorCS"),sQuery(id+"F0.wireOp",EDGE,"E51.MirrorCS"),sQuery(id+"F0.wireOp",EDGE,"E52.MirrorCS"),sQuery(id+"F0.wireOp",EDGE,"E73.0"),sQuery(id+"F0.wireOp",EDGE,"E74"),sQuery(id+"F0.wireOp",EDGE,"E75")])]});
            hole(context, id + "F4", {"style" : HoleStyle.SIMPLE, "endStyle" : HoleEndStyle.THROUGH, "oppositeDirection" : true, "standardTappedOrClearance" : lookupTablePath({ "standard" : "ANSI", "engagement" : "75%", "pitch" : "20 tpi", "size" : "1/4", "type" : "Tapped" }), "standardBlindInLast" : lookupTablePath({ "standard" : "ANSI", "engagement" : "75%", "pitch" : "20 tpi", "size" : "1/4", "type" : "Tapped" }), "holeDiameter" : 5.1 * mm, "majorDiameter" : 6.35 * mm, "showTappedDepth" : true, "isTappedThrough" : true, "tappedDepth" : 12.7 * mm, "tapClearance" : 3, "locations" : qUnion([Q0, Q1, Q2, Q3]), "scope" : qUnion([Q4])});
        }
    });
